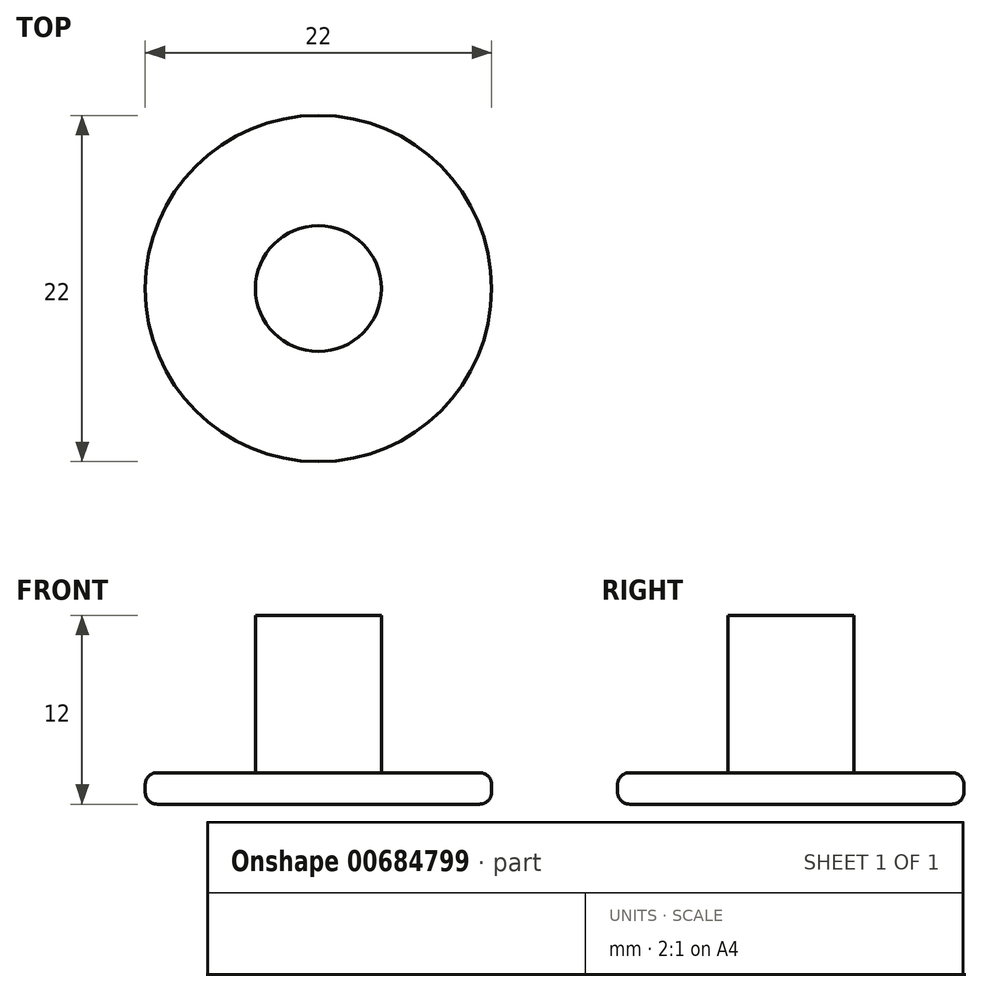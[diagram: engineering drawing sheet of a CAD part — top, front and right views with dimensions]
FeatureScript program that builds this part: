
annotation { "Feature Type Name" : "Feature", "Feature Type Description" : "" }
export const myFeature = defineFeature(function(context is Context, id is Id, definition is map)
    precondition{}
    {
        {
            var Q0;
            Q0=qCreatedBy(makeId("Top.planeOp"),FACE);
            var sketch = newSketch(context, id + "F0", { "sketchPlane" : qUnion([Q0])});
            skCircle(sketch, "E0", {"center": v(0, 0) * mm, "radius": 11 * mm});
            skPoint(sketch, "E1.10.internal.orphan", {"position": v(0, -6.53) * mm});
            skLineSegment(sketch, "E2", {"start": v(0, 9.32) * mm, "end": v(0, 0) * mm});
            skLineSegment(sketch, "E3", {"start": v(0, 0) * mm, "end": v(0, -7.73) * mm});
            skSolve(sketch);
        }
        {
            var Q0;
            Q0=qSketchRegion(id+"F0",true);
            extrude(context, id + "F1", {"entities" : qUnion([Q0]), "depth" : 2 * mm, "offsetDistance" : 25.4 * mm});
        }
        {
            var Q0;
            Q0=qCreatedBy(makeId("Top.planeOp"),FACE);
            var sketch = newSketch(context, id + "F2", { "sketchPlane" : qUnion([Q0])});
            skCircle(sketch, "E4", {"center": v(0, 0) * mm, "radius": 4 * mm});
            skSolve(sketch);
        }
        {
            var Q0;
            Q0=makeQuery(id+"F2.imprint","IMPRINT",FACE,{"disambiguationData":[TD([[makeQuery(id+"F2.imprint","IMPRINT",EDGE,{"derivedFrom":sQuery(id+"F2.wireOp",EDGE,"E4")}),1.0]])]});
            extrude(context, id + "F3", {"entities" : qUnion([Q0]), "operationType" : NewBodyOperationType.ADD, "depth" : 12 * mm, "offsetDistance" : 25.4 * mm});
        }
        {
            var Q0;
            Q0=makeQuery(id+"F1.opExtrude","CAP_EDGE",EDGE,{"disambiguationData":[OSD([sQuery(id+"F0.wireOp",EDGE,"E0")])],"isStart":false});
            var Q1;
            Q1=makeQuery(id+"F1.opExtrude","SWEPT_FACE",FACE,{"disambiguationData":[OSD([sQuery(id+"F0.wireOp",EDGE,"E0")])]});
            fillet(context, id + "F4", {"entities" : qUnion([Q0, Q1]), "radius" : 0.76 * mm, "tangentPropagation" : true, "allowEdgeOverflow" : false});
        }
    });
